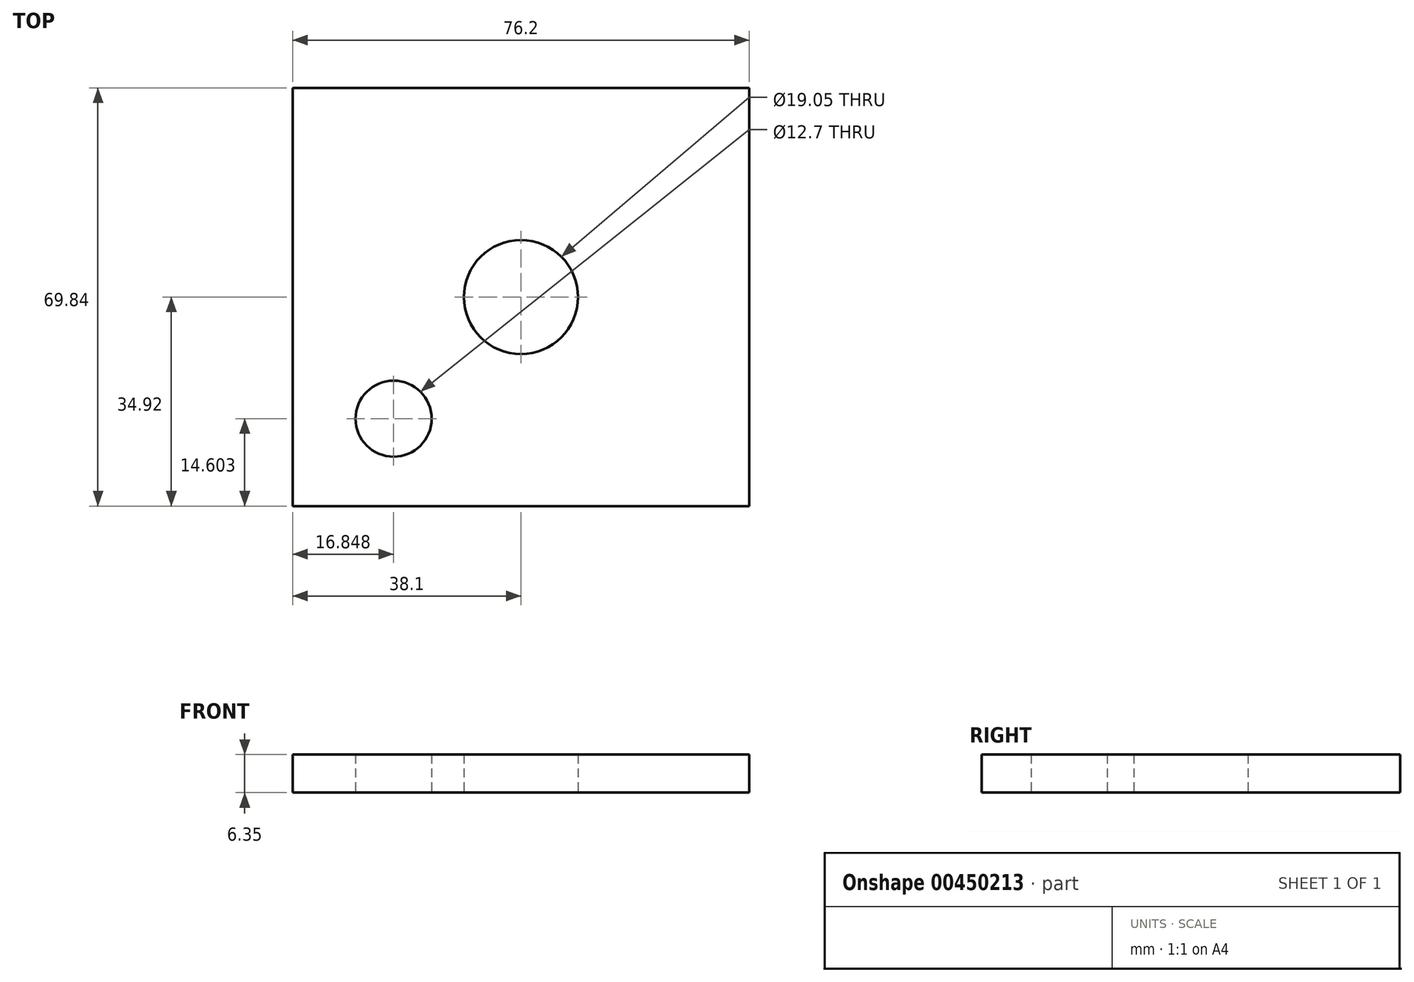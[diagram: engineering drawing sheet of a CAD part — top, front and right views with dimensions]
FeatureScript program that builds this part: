
annotation { "Feature Type Name" : "Feature", "Feature Type Description" : "" }
export const myFeature = defineFeature(function(context is Context, id is Id, definition is map)
    precondition{}
    {
        {
            var Q0;
            Q0=qCreatedBy(makeId("Top.planeOp"),FACE);
            var sketch = newSketch(context, id + "F0", { "sketchPlane" : qUnion([Q0])});
            skLineSegment(sketch, "E0.bottom", {"start": v(-38.1, 34.93) * mm, "end": v(38.1, 34.93) * mm});
            skLineSegment(sketch, "E0.top", {"start": v(-38.1, -34.93) * mm, "end": v(38.1, -34.93) * mm});
            skLineSegment(sketch, "E0.left", {"start": v(-38.1, 34.93) * mm, "end": v(-38.1, -34.92) * mm});
            skLineSegment(sketch, "E0.right", {"start": v(38.1, 34.93) * mm, "end": v(38.1, -34.92) * mm});
            skPoint(sketch, "E0.middle", {"position": v(0, 0) * mm});
            skCircle(sketch, "E1", {"center": v(0, 0) * mm, "radius": 9.53 * mm});
            skCircle(sketch, "E2", {"center": v(-21.25, -20.32) * mm, "radius": 6.35 * mm});
            skSolve(sketch);
        }
        {
            var Q0;
            Q0=makeQuery(id+"F0.imprint","IMPRINT",FACE,{"disambiguationData":[TD([[makeQuery(id+"F0.imprint","IMPRINT",EDGE,{"derivedFrom":sQuery(id+"F0.wireOp",EDGE,"E0.bottom")}),-1.0]])]});
            extrude(context, id + "F1", {"entities" : qUnion([Q0]), "depth" : 6.35 * mm});
        }
    });
